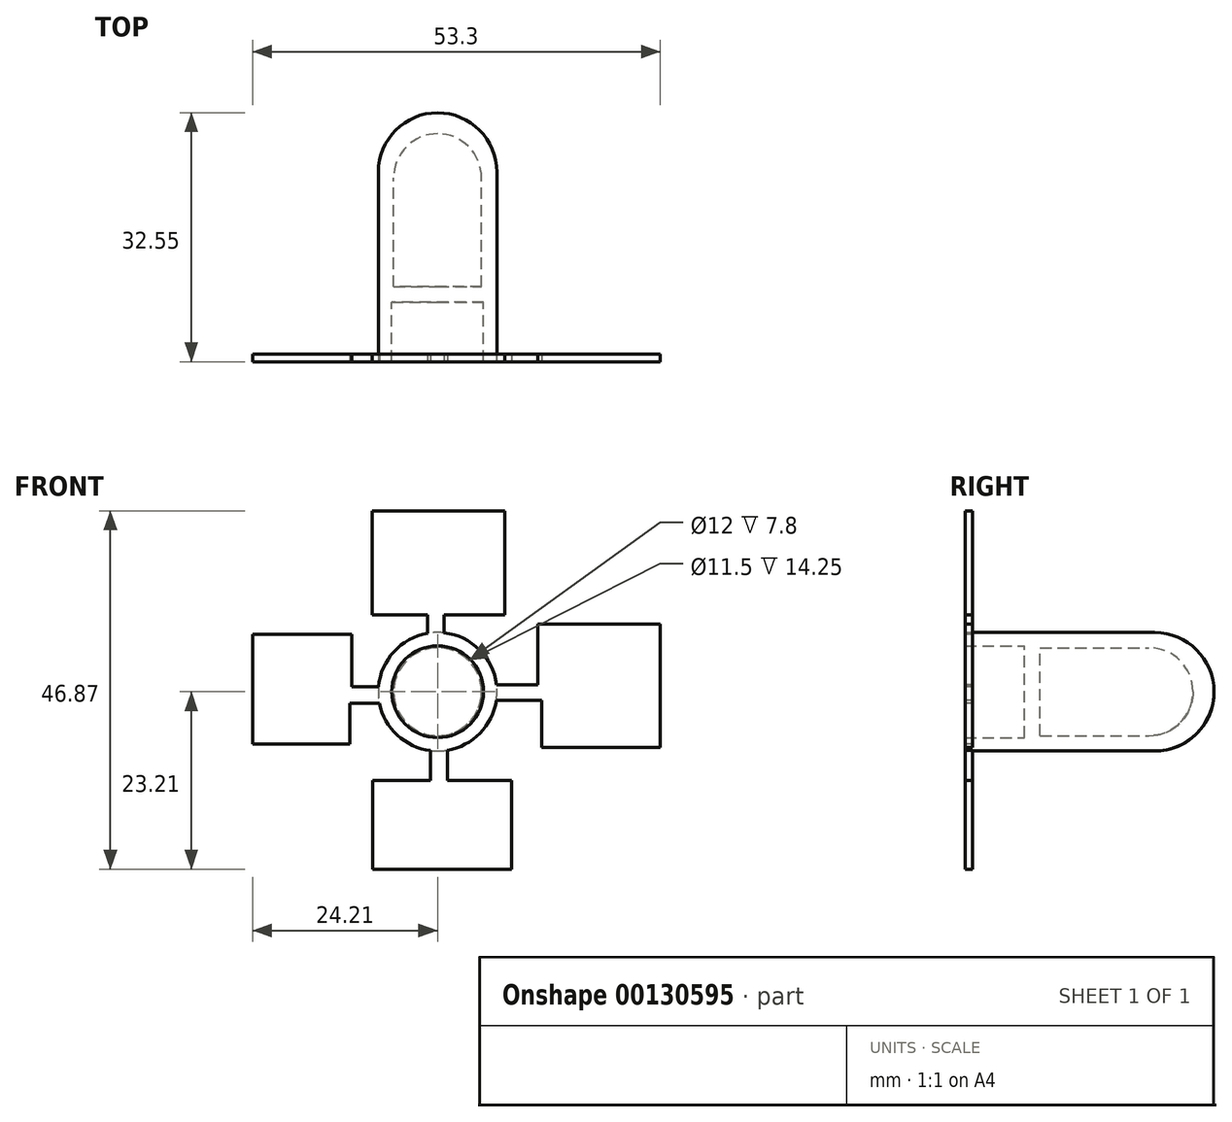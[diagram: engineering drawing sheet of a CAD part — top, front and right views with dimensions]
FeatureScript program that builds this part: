
annotation { "Feature Type Name" : "Feature", "Feature Type Description" : "" }
export const myFeature = defineFeature(function(context is Context, id is Id, definition is map)
    precondition{}
    {
        {
            var Q0;
            Q0=qCreatedBy(makeId("Front.planeOp"),FACE);
            var sketch = newSketch(context, id + "F0", { "sketchPlane" : qUnion([Q0])});
            skCircle(sketch, "E0", {"center": v(0, 0) * mm, "radius": 7.75 * mm});
            skCircle(sketch, "E1", {"center": v(0, 0) * mm, "radius": 5.75 * mm});
            skSolve(sketch);
        }
        {
            var Q0;
            Q0=makeQuery(id+"F0.imprint","IMPRINT",FACE,{"disambiguationData":[TD([[makeQuery(id+"F0.imprint","IMPRINT",EDGE,{"derivedFrom":sQuery(id+"F0.wireOp",EDGE,"E0")}),1.0]])]});
            var Q1;
            Q1=makeQuery(id+"F0.imprint","IMPRINT",FACE,{"disambiguationData":[TD([[makeQuery(id+"F0.imprint","IMPRINT",EDGE,{"derivedFrom":sQuery(id+"F0.wireOp",EDGE,"E1")}),1.0]])]});
            extrude(context, id + "F1", {"entities" : qUnion([Q0, Q1]), "oppositeDirection" : true, "depth" : 7.75 * mm});
        }
        {
            var Q0;
            Q0=makeQuery(id+"F1.opExtrude","CAP_EDGE",EDGE,{"disambiguationData":[OSD([sQuery(id+"F0.wireOp",EDGE,"E0")])],"isStart":false});
            fillet(context, id + "F2", {"entities" : qUnion([Q0]), "radius" : 7.75 * mm, "tangentPropagation" : true, "allowEdgeOverflow" : false});
        }
        {
            var Q0;
            Q0=makeQuery(id+"F0.imprint","IMPRINT",FACE,{"disambiguationData":[TD([[makeQuery(id+"F0.imprint","IMPRINT",EDGE,{"derivedFrom":sQuery(id+"F0.wireOp",EDGE,"E0")}),1.0]])]});
            extrude(context, id + "F3", {"entities" : qUnion([Q0]), "operationType" : NewBodyOperationType.ADD, "depth" : 15 * mm});
        }
        {
            var Q0;
            Q0=makeQuery(id+"F0.imprint","IMPRINT",FACE,{"disambiguationData":[TD([[makeQuery(id+"F0.imprint","IMPRINT",EDGE,{"derivedFrom":sQuery(id+"F0.wireOp",EDGE,"E1")}),1.0]])]});
            extrude(context, id + "F4", {"entities" : qUnion([Q0]), "operationType" : NewBodyOperationType.REMOVE, "oppositeDirection" : true, "depth" : 5 * mm});
        }
        {
            var Q0;
            Q0=makeQuery(id+"F4.boolean.opBoolean","COPY",EDGE,{"derivedFrom":makeQuery(id+"F4.opExtrude","CAP_EDGE",EDGE,{"disambiguationData":[OSD([sQuery(id+"F0.wireOp",EDGE,"E1")])],"isStart":false})});
            fillet(context, id + "F5", {"entities" : qUnion([Q0]), "radius" : 5.75 * mm, "tangentPropagation" : true, "allowEdgeOverflow" : false});
        }
        {
            var Q0;
            Q0=makeQuery(id+"F3.opExtrude","CAP_FACE",FACE,{"disambiguationData":[OSD([sQuery(id+"F0.wireOp",EDGE,"E0"),sQuery(id+"F0.wireOp",EDGE,"E1")])],"isStart":false});
            var sketch = newSketch(context, id + "F6", { "sketchPlane" : qUnion([Q0])});
            skCircle(sketch, "E2", {"center": v(0, 0) * mm, "radius": 6 * mm});
            skSolve(sketch);
        }
        {
            var Q0;
            Q0=makeQuery(id+"F6.imprint","IMPRINT",FACE,{"disambiguationData":[TD([[makeQuery(id+"F6.imprint","IMPRINT",EDGE,{"derivedFrom":sQuery(id+"F6.wireOp",EDGE,"E2")}),-1.0]])]});
            extrude(context, id + "F7", {"entities" : qUnion([Q0]), "operationType" : NewBodyOperationType.ADD, "depth" : 9.8 * mm});
        }
        {
            var Q0;
            Q0=makeQuery(id+"F6.imprint","IMPRINT",FACE,{"disambiguationData":[TD([[makeQuery(id+"F6.imprint","IMPRINT",EDGE,{"derivedFrom":sQuery(id+"F6.wireOp",EDGE,"E2")}),1.0]])]});
            var Q1;
            Q1=makeQuery(id+"F6.imprint","IMPRINT",FACE,{"disambiguationData":[TD([[makeQuery(id+"F6.imprint","IMPRINT",EDGE,{"derivedFrom":makeQuery(id+"F3.opExtrude","CAP_EDGE",EDGE,{"disambiguationData":[OSD([sQuery(id+"F0.wireOp",EDGE,"E1")])],"isStart":false})}),1.0]])]});
            extrude(context, id + "F8", {"entities" : qUnion([Q0, Q1]), "operationType" : NewBodyOperationType.ADD, "depth" : 2 * mm});
        }
        {
            var Q0;
            Q0=makeQuery(id+"F7.opExtrude","CAP_FACE",FACE,{"disambiguationData":[OSD([sQuery(id+"F0.wireOp",EDGE,"E0"),sQuery(id+"F6.wireOp",EDGE,"E2")])],"isStart":false});
            var sketch = newSketch(context, id + "F9", { "sketchPlane" : qUnion([Q0])});
            skLineSegment(sketch, "E3", {"start": v(0.85, 7.7) * mm, "end": v(0.85, 10.03) * mm});
            skLineSegment(sketch, "E4", {"start": v(0.85, 10.03) * mm, "end": v(8.75, 10.03) * mm});
            skLineSegment(sketch, "E5", {"start": v(8.75, 10.03) * mm, "end": v(8.75, 23.66) * mm});
            skLineSegment(sketch, "E6", {"start": v(8.75, 23.66) * mm, "end": v(-8.54, 23.66) * mm});
            skLineSegment(sketch, "E7", {"start": v(-8.54, 23.66) * mm, "end": v(-8.54, 10.27) * mm});
            skLineSegment(sketch, "E8", {"start": v(-8.54, 10.27) * mm, "end": v(-8.54, 10.03) * mm});
            skLineSegment(sketch, "E9", {"start": v(-8.54, 10.03) * mm, "end": v(-1.32, 10.03) * mm});
            skLineSegment(sketch, "E10", {"start": v(-1.32, 10.03) * mm, "end": v(-1.32, 7.64) * mm});
            skLineSegment(sketch, "E11", {"start": v(-7.72, 0.63) * mm, "end": v(-11.2, 0.63) * mm});
            skLineSegment(sketch, "E12", {"start": v(-11.2, 0.63) * mm, "end": v(-11.2, 7.51) * mm});
            skLineSegment(sketch, "E13", {"start": v(-11.2, 7.51) * mm, "end": v(-24.21, 7.51) * mm});
            skLineSegment(sketch, "E14", {"start": v(-24.21, 7.51) * mm, "end": v(-24.21, -6.85) * mm});
            skLineSegment(sketch, "E15", {"start": v(-24.21, -6.85) * mm, "end": v(-11.47, -6.85) * mm});
            skLineSegment(sketch, "E16", {"start": v(-11.47, -6.85) * mm, "end": v(-11.47, -1.5) * mm});
            skLineSegment(sketch, "E17", {"start": v(-11.47, -1.5) * mm, "end": v(-7.6, -1.5) * mm});
            skLineSegment(sketch, "E18", {"start": v(-0.93, -7.7) * mm, "end": v(-0.93, -11.6) * mm});
            skLineSegment(sketch, "E19", {"start": v(-0.93, -11.6) * mm, "end": v(-8.49, -11.6) * mm});
            skLineSegment(sketch, "E20", {"start": v(-8.49, -11.6) * mm, "end": v(-8.49, -23.21) * mm});
            skLineSegment(sketch, "E21", {"start": v(-8.49, -23.21) * mm, "end": v(9.7, -23.21) * mm});
            skLineSegment(sketch, "E22", {"start": v(9.7, -23.21) * mm, "end": v(9.7, -11.6) * mm});
            skLineSegment(sketch, "E23", {"start": v(9.7, -11.6) * mm, "end": v(1.26, -11.6) * mm});
            skLineSegment(sketch, "E24", {"start": v(1.26, -11.6) * mm, "end": v(1.26, -7.65) * mm});
            skLineSegment(sketch, "E25", {"start": v(7.7, 0.93) * mm, "end": v(13.08, 0.93) * mm});
            skLineSegment(sketch, "E26", {"start": v(13.08, 0.93) * mm, "end": v(13.08, 8.83) * mm});
            skLineSegment(sketch, "E27", {"start": v(13.08, 8.83) * mm, "end": v(29.1, 8.83) * mm});
            skLineSegment(sketch, "E28", {"start": v(29.1, 8.83) * mm, "end": v(29.1, -7.3) * mm});
            skLineSegment(sketch, "E29", {"start": v(29.1, -7.3) * mm, "end": v(13.63, -7.3) * mm});
            skLineSegment(sketch, "E30", {"start": v(13.63, -7.3) * mm, "end": v(13.63, -1.13) * mm});
            skLineSegment(sketch, "E31", {"start": v(13.63, -1.13) * mm, "end": v(7.67, -1.13) * mm});
            skSolve(sketch);
        }
        {
            var Q0;
            {var subQ0=sQuery(id+"F9.wireOp",EDGE,"E11");Q0=makeQuery(id+"F9.imprint","IMPRINT",FACE,{"disambiguationData":[TD([[makeQuery(id+"F9.imprint","IMPRINT",EDGE,{"derivedFrom":subQ0}),1.0]])]});}
            var Q1;
            {var subQ0=sQuery(id+"F9.wireOp",EDGE,"E3");Q1=makeQuery(id+"F9.imprint","IMPRINT",FACE,{"disambiguationData":[TD([[makeQuery(id+"F9.imprint","IMPRINT",EDGE,{"derivedFrom":subQ0}),1.0]])]});}
            var Q2;
            {var subQ0=sQuery(id+"F9.wireOp",EDGE,"E25");Q2=makeQuery(id+"F9.imprint","IMPRINT",FACE,{"disambiguationData":[TD([[makeQuery(id+"F9.imprint","IMPRINT",EDGE,{"derivedFrom":subQ0}),-1.0]])]});}
            var Q3;
            {var subQ0=sQuery(id+"F9.wireOp",EDGE,"E18");Q3=makeQuery(id+"F9.imprint","IMPRINT",FACE,{"disambiguationData":[TD([[makeQuery(id+"F9.imprint","IMPRINT",EDGE,{"derivedFrom":subQ0}),1.0]])]});}
            extrude(context, id + "F10", {"entities" : qUnion([Q0, Q1, Q2, Q3]), "operationType" : NewBodyOperationType.ADD, "oppositeDirection" : true, "depth" : 1 * mm});
        }
    });
